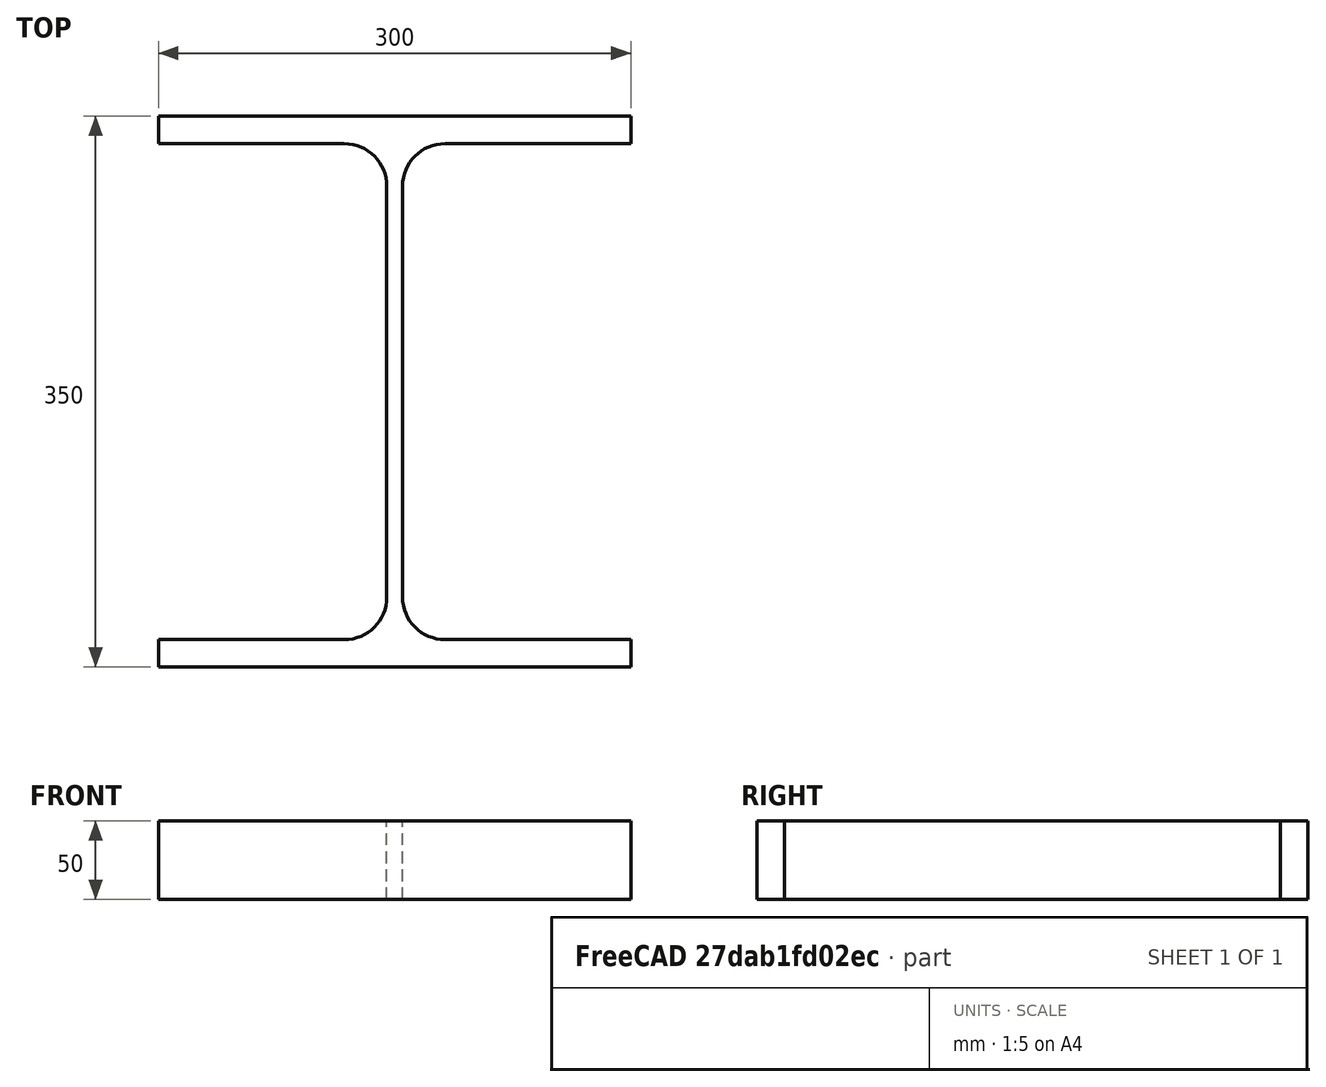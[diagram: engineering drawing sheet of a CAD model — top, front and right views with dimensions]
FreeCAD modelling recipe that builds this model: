
FCSTD DOCUMENT  (FreeCAD 0.15R4671 (Git))
Label: HE-A-Profile 360 DIN1025-3 S235JR
License: All rights reserved
LicenseURL: http://en.wikipedia.org/wiki/All_rights_reserved
objects: Sketcher::SketchObject×1, Part::Extrusion×1
note: 2 computed .brp shape members not serialized (recipe doc carries the construction recipe); baked Part::Feature solids carry a one-line shape summary decoded from their .brp

FEATURE [Sketcher::SketchObject] Sketch
  sketch-geometry (16):
    g0: LineSegment StartX=5 StartY=-130.5 StartZ=0 EndX=5 EndY=130.5 EndZ=0
    g1: LineSegment StartX=32 StartY=157.5 StartZ=0 EndX=150 EndY=157.5 EndZ=0
    g2: LineSegment StartX=150 StartY=157.5 StartZ=0 EndX=150 EndY=175 EndZ=0
    g3: LineSegment StartX=150 StartY=175 StartZ=0 EndX=-150 EndY=175 EndZ=0
    g4: LineSegment StartX=-150 StartY=175 StartZ=0 EndX=-150 EndY=157.5 EndZ=0
    g5: LineSegment StartX=-150 StartY=157.5 StartZ=0 EndX=-32 EndY=157.5 EndZ=0
    g6: LineSegment StartX=-5 StartY=130.5 StartZ=0 EndX=-5 EndY=-130.5 EndZ=0
    g7: LineSegment StartX=-32 StartY=-157.5 StartZ=0 EndX=-150 EndY=-157.5 EndZ=0
    g8: LineSegment StartX=-150 StartY=-157.5 StartZ=0 EndX=-150 EndY=-175 EndZ=0
    g9: LineSegment StartX=-150 StartY=-175 StartZ=0 EndX=150 EndY=-175 EndZ=0
    g10: LineSegment StartX=150 StartY=-175 StartZ=0 EndX=150 EndY=-157.5 EndZ=0
    g11: LineSegment StartX=150 StartY=-157.5 StartZ=0 EndX=32 EndY=-157.5 EndZ=0
    g12: ArcOfCircle CenterX=32 CenterY=130.5 CenterZ=0 NormalX=0 NormalY=0 NormalZ=1 Radius=27 StartAngle=1.5708 EndAngle=3.14159
    g13: ArcOfCircle CenterX=32 CenterY=-130.5 CenterZ=0 NormalX=0 NormalY=0 NormalZ=1 Radius=27 StartAngle=3.14159 EndAngle=4.71239
    g14: ArcOfCircle CenterX=-32 CenterY=130.5 CenterZ=0 NormalX=0 NormalY=0 NormalZ=1 Radius=27 StartAngle=0 EndAngle=1.5708
    g15: ArcOfCircle CenterX=-32 CenterY=-130.5 CenterZ=0 NormalX=0 NormalY=0 NormalZ=1 Radius=27 StartAngle=4.71239 EndAngle=6.28319
  constraints (42):
    c: Vertical(g0)
    c: Coincident(g2,g1)
    c: Vertical(g2)
    c: Coincident(g3,g2)
    c: Coincident(g4,g3)
    c: Vertical(g4)
    c: Coincident(g5,g4)
    c: Horizontal(g5)
    c: Vertical(g6)
    c: Horizontal(g7)
    c: Coincident(g8,g7)
    c: Vertical(g8)
    c: Coincident(g9,g8)
    c: Horizontal(g9)
    c: Coincident(g10,g9)
    c: Vertical(g10)
    c: Coincident(g11,g10)
    c: Horizontal(g11)
    c: Tangent(g1,g12) = 1.5708
    c: Tangent(g0,g12) = 1.5708
    c: Tangent(g0,g13) = 1.5708
    c: Tangent(g11,g13) = 1.5708
    c: Tangent(g5,g14) = 1.5708
    c: Tangent(g6,g14) = 1.5708
    c: Tangent(g6,g15) = 1.5708
    c: Tangent(g7,g15) = 1.5708
    c: Equal(g3,g9)
    c: Equal(g2,g4)
    c: Equal(g4,g8)
    c: Equal(g8,g10)
    c: Equal(g12,g14)
    c: Equal(g14,g15)
    c: Equal(g15,g13)
    c: Symmetric(g2,g3,g-2)
    c: Symmetric(g9,g8,g-2)
    c: Symmetric(g0,g6,g-2)
    c: Symmetric(g2,g9,g-1)
    c: DistanceY(g2,g9) = -350
    c: DistanceX(g3) = -300
    c: DistanceX(g0,g6) = -10
    c: DistanceY(g2) = 17.5
    c: Radius(g12) = 27
FEATURE [Part::Extrusion] Extrude  label="HE-A-Profile 360 DIN1025-3 S235JR"
  Base = -> Sketch
  Dir = (0,0,50)
  Solid = true
